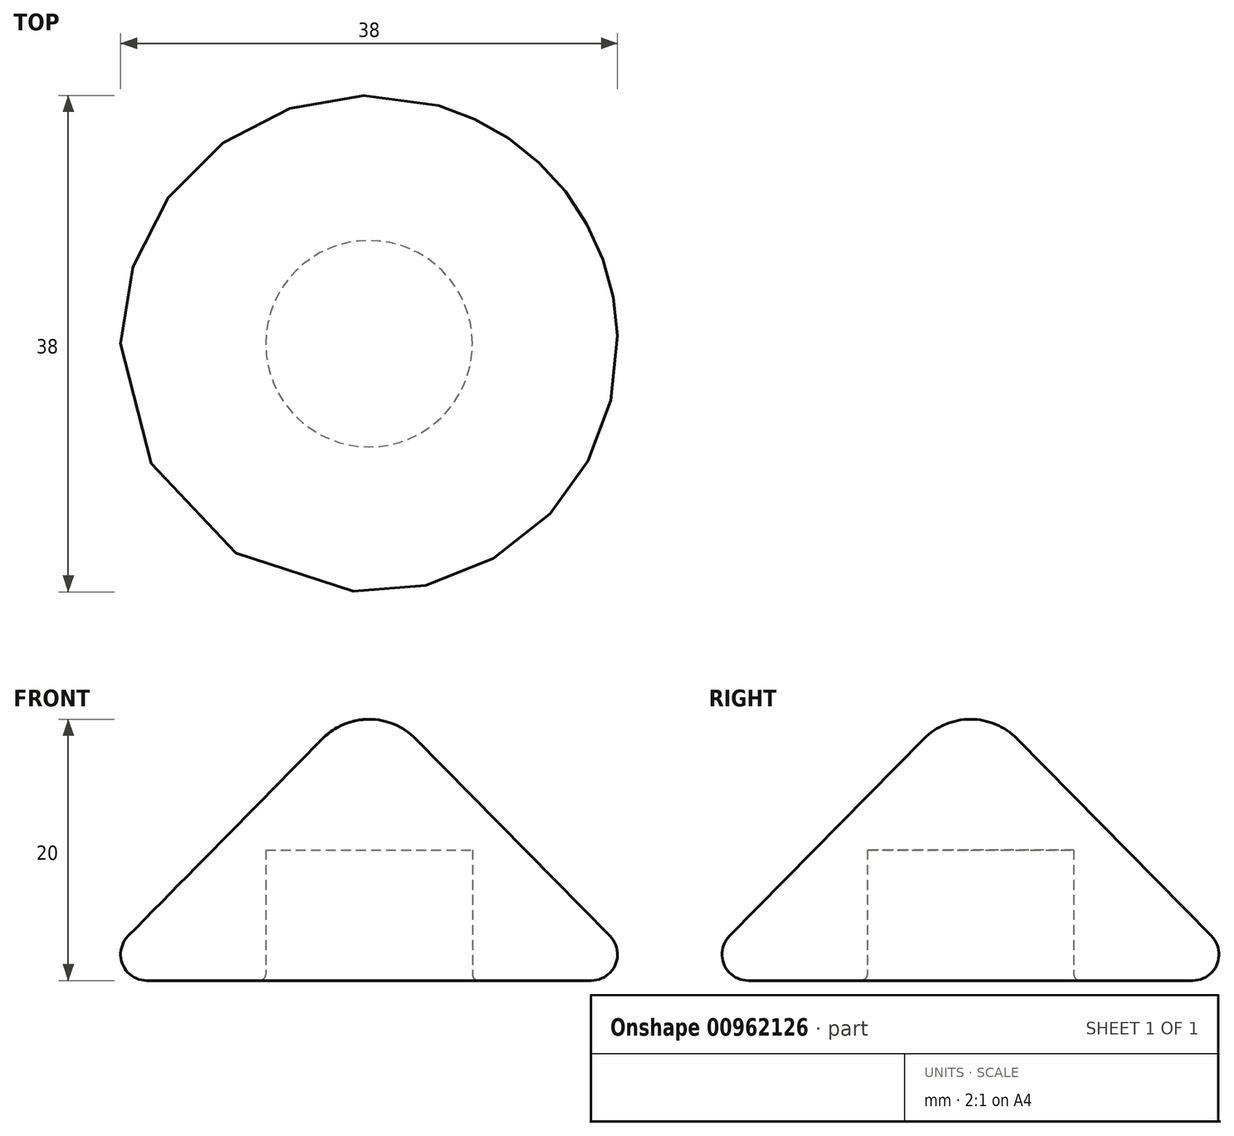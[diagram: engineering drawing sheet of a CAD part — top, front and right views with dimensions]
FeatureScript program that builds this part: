
annotation { "Feature Type Name" : "Feature", "Feature Type Description" : "" }
export const myFeature = defineFeature(function(context is Context, id is Id, definition is map)
    precondition{}
    {
        {
            var Q0;
            Q0=qCreatedBy(makeId("Front.planeOp"),FACE);
            var sketch = newSketch(context, id + "F0", { "sketchPlane" : qUnion([Q0])});
            skLineSegment(sketch, "E0", {"start": v(0, 10) * mm, "end": v(0, 20) * mm});
            skArc(sketch, "E1", {"start": v(0, 20) * mm, "mid": v(-1.93, 19.61) * mm, "end": v(-3.56, 18.5) * mm});
            skLineSegment(sketch, "E2", {"start": v(-7.9, 0) * mm, "end": v(-17, 0) * mm});
            skArc(sketch, "E3", {"start": v(-18.43, 3.4) * mm, "mid": v(-18.84, 1.23) * mm, "end": v(-17, 0) * mm});
            skLineSegment(sketch, "E4", {"start": v(-18.43, 3.4) * mm, "end": v(-3.56, 18.5) * mm});
            skLineSegment(sketch, "E5", {"start": v(-7.9, 0) * mm, "end": v(-7.9, 10) * mm});
            skLineSegment(sketch, "E6", {"start": v(-7.9, 10) * mm, "end": v(0, 10) * mm});
            skSolve(sketch);
        }
        {
            var Q0;
            Q0=makeQuery(id+"F0.imprint","IMPRINT",FACE,{"disambiguationData":[TD([[makeQuery(id+"F0.imprint","IMPRINT",EDGE,{"derivedFrom":sQuery(id+"F0.wireOp",EDGE,"E0")}),1.0]])]});
            var Q1;
            Q1=sQuery(id+"F0.wireOp",EDGE,"E0");
            revolve(context, id + "F1", {"surfaceOperationType" : NewSurfaceOperationType.NEW, "entities" : qUnion([Q0]), "axis" : qUnion([Q1]), "revolveType" : RevolveType.FULL});
        }
        {
            var Q0;
            Q0=makeQuery(id+"F1.opRevolve","SWEPT_EDGE",EDGE,{"disambiguationData":[OSD([sQuery(id+"F0.wireOp",EDGE,"E2"),sQuery(id+"F0.wireOp",EDGE,"E5")])]});
            fillet(context, id + "F2", {"entities" : qUnion([Q0]), "radius" : .5 * mm, "tangentPropagation" : true, "defaultsChanged" : false, "vertexSettings" : [], "allowEdgeOverflow" : false});
        }
    });
